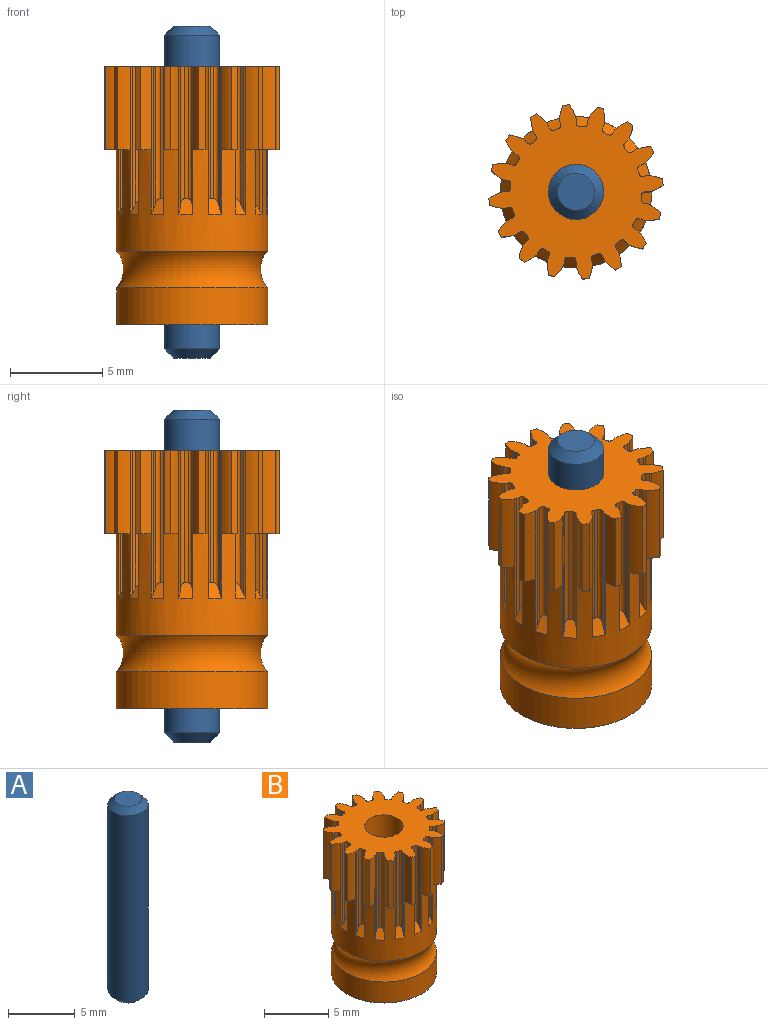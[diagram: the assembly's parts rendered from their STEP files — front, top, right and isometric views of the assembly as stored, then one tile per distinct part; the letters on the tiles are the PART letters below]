
ASSEMBLY  parts=2 mates=1
PART A: 5 faces, bbox 3x3x18 mm
  f0: cylinder r=1.5mm len=17mm, axis (0,0,-1), area 160.2mm2, adj f3,f4
  f1: plane 2x2mm, normal (0,0,1), area 3.1mm2, adj f4
  f2: plane 2x2mm, normal (0,0,-1), area 3.1mm2, adj f3
  f3: cone r=1.5mm half-angle=45deg, axis (0,0,1), area 5.6mm2, adj f0,f2
  f4: cone r=1mm half-angle=45deg, axis (0,0,-1), area 5.6mm2, adj f0,f1
PART B: 198 faces, bbox 9.5x9.5x14 mm
  f0: cylinder r=4.1mm len=8.2mm, axis (0,0,-1), area 100mm2, adj f5,f11,f12,f13,f19,f20,f26,f27
  f1: cylinder r=4.1mm len=8.2mm, axis (0,0,-1), area 51.5mm2, adj f4,f181
  f2: plane 9.45x9.45mm, normal (0,0,1), area 47mm2, adj f3,f5,f6,f7,f8,f9,f10,f11
  f3: cylinder r=1.5mm len=14mm, axis (0,0,-1), area 131.9mm2, adj f2,f4
  f4: plane 8.2x8.2mm, normal (0,0,-1), area 45.7mm2, adj f1,f3
  f5: plane 8x0.12mm, normal (0.97,0.24,0), area 1mm2, adj f0,f2,f6,f117,f188
  f6: plane 7.82x0.23mm, normal (1,0,0), area 1.8mm2, adj f2,f5,f7,f188
  f7: cylinder r=0.2mm len=7.46mm, axis (0,0,1), area 2.2mm2, adj f2,f6,f8,f188
  f8: plane 7.17x0.23mm, normal (0.09,1,0), area 1.6mm2, adj f2,f7,f9,f188
  f9: cylinder r=0.2mm len=7.46mm, axis (0,0,1), area 2.2mm2, adj f2,f8,f10,f188
  f10: plane 7.82x0.23mm, normal (-0.98,0.17,0), area 1.8mm2, adj f2,f9,f11,f188
  f11: plane 8x0.11mm, normal (-0.91,0.41,0), area 1mm2, adj f0,f2,f10,f177,f188
  f12: plane 8x0.09mm, normal (-0.69,0.73,0), area 1mm2, adj f0,f2,f18,f173,f189
  f13: plane 8x0.12mm, normal (0.99,-0.15,0), area 1mm2, adj f0,f2,f14,f178,f189
  f14: plane 7.82x0.21mm, normal (0.92,-0.38,0), area 1.8mm2, adj f2,f13,f15,f189
  f15: cylinder r=0.2mm len=7.46mm, axis (0,0,1), area 2.2mm2, adj f2,f14,f16,f189
  f16: plane 7.17x0.2mm, normal (0.46,0.89,0), area 1.6mm2, adj f2,f15,f17,f189
  f17: cylinder r=0.2mm len=7.46mm, axis (0,0,1), area 2.2mm2, adj f2,f16,f18,f189
  f18: plane 7.82x0.2mm, normal (-0.84,0.54,0), area 1.8mm2, adj f2,f12,f17,f189
  f19: plane 8x0.12mm, normal (-0.36,0.93,0), area 1mm2, adj f0,f2,f25,f169,f190
  f20: plane 8x0.11mm, normal (0.86,-0.52,0), area 1mm2, adj f0,f2,f21,f174,f190
  f21: plane 7.82x0.16mm, normal (0.71,-0.71,0), area 1.8mm2, adj f2,f20,f22,f190
  f22: cylinder r=0.2mm len=7.46mm, axis (0,0,1), area 2.2mm2, adj f2,f21,f23,f190
  f23: plane 7.17x0.18mm, normal (0.77,0.64,0), area 1.6mm2, adj f2,f22,f24,f190
  f24: cylinder r=0.2mm len=7.46mm, axis (0,0,1), area 2.2mm2, adj f2,f23,f25,f190
  f25: plane 7.82x0.19mm, normal (-0.57,0.82,0), area 1.8mm2, adj f2,f19,f24,f190
  f26: plane 8x0.12mm, normal (0.03,1,0), area 1mm2, adj f0,f2,f32,f165,f191
  f27: plane 8x0.1mm, normal (0.59,-0.8,0), area 1mm2, adj f0,f2,f28,f170,f191
  f28: plane 7.82x0.21mm, normal (0.38,-0.92,0), area 1.8mm2, adj f2,f27,f29,f191
  f29: cylinder r=0.2mm len=7.46mm, axis (0,0,1), area 2.2mm2, adj f2,f28,f30,f191
  f30: plane 7.17x0.22mm, normal (0.95,0.3,0), area 1.6mm2, adj f2,f29,f31,f191
  f31: cylinder r=0.2mm len=7.46mm, axis (0,0,1), area 2.2mm2, adj f2,f30,f32,f191
  f32: plane 7.82x0.23mm, normal (-0.22,0.98,0), area 1.8mm2, adj f2,f26,f31,f191
  f33: plane 8x0.11mm, normal (0.41,0.91,0), area 1mm2, adj f0,f2,f39,f161,f192
  f34: plane 8x0.12mm, normal (0.24,-0.97,0), area 1mm2, adj f0,f2,f35,f166,f192
  f35: plane 7.82x0.23mm, normal (0,-1,0), area 1.8mm2, adj f2,f34,f36,f192
  f36: cylinder r=0.2mm len=7.46mm, axis (0,0,1), area 2.2mm2, adj f2,f35,f37,f192
  f37: plane 7.17x0.23mm, normal (1,-0.09,0), area 1.6mm2, adj f2,f36,f38,f192
  f38: cylinder r=0.2mm len=7.46mm, axis (0,0,1), area 2.2mm2, adj f2,f37,f39,f192
  f39: plane 7.82x0.23mm, normal (0.17,0.98,0), area 1.8mm2, adj f2,f33,f38,f192
  f40: plane 8x0.09mm, normal (0.73,0.69,0), area 1mm2, adj f0,f2,f46,f157,f193
  f41: plane 8x0.12mm, normal (-0.15,-0.99,0), area 1mm2, adj f0,f2,f42,f162,f193
  f42: plane 7.82x0.21mm, normal (-0.38,-0.92,0), area 1.8mm2, adj f2,f41,f43,f193
  f43: cylinder r=0.2mm len=7.46mm, axis (0,0,1), area 2.2mm2, adj f2,f42,f44,f193
  f44: plane 7.17x0.2mm, normal (0.89,-0.46,0), area 1.6mm2, adj f2,f43,f45,f193
  f45: cylinder r=0.2mm len=7.46mm, axis (0,0,1), area 2.2mm2, adj f2,f44,f46,f193
  f46: plane 7.82x0.2mm, normal (0.54,0.84,0), area 1.8mm2, adj f2,f40,f45,f193
  f47: plane 8x0.12mm, normal (0.93,0.36,0), area 1mm2, adj f0,f2,f53,f153,f194
  f48: plane 8x0.11mm, normal (-0.52,-0.86,0), area 1mm2, adj f0,f2,f49,f158,f194
  f49: plane 7.82x0.16mm, normal (-0.71,-0.71,0), area 1.8mm2, adj f2,f48,f50,f194
  f50: cylinder r=0.2mm len=7.46mm, axis (0,0,1), area 2.2mm2, adj f2,f49,f51,f194
  f51: plane 7.17x0.18mm, normal (0.64,-0.77,0), area 1.6mm2, adj f2,f50,f52,f194
  f52: cylinder r=0.2mm len=7.46mm, axis (0,0,1), area 2.2mm2, adj f2,f51,f53,f194
  f53: plane 7.82x0.19mm, normal (0.82,0.57,0), area 1.8mm2, adj f2,f47,f52,f194
  f54: plane 8x0.12mm, normal (1,-0.03,0), area 1mm2, adj f0,f2,f60,f149,f195
  f55: plane 8x0.1mm, normal (-0.8,-0.59,0), area 1mm2, adj f0,f2,f56,f154,f195
  f56: plane 7.82x0.21mm, normal (-0.92,-0.38,0), area 1.8mm2, adj f2,f55,f57,f195
  f57: cylinder r=0.2mm len=7.46mm, axis (0,0,1), area 2.2mm2, adj f2,f56,f58,f195
  f58: plane 7.17x0.22mm, normal (0.3,-0.95,0), area 1.6mm2, adj f2,f57,f59,f195
  f59: cylinder r=0.2mm len=7.46mm, axis (0,0,1), area 2.2mm2, adj f2,f58,f60,f195
  f60: plane 7.82x0.23mm, normal (0.98,0.22,0), area 1.8mm2, adj f2,f54,f59,f195
  f61: plane 8x0.11mm, normal (0.91,-0.41,0), area 1mm2, adj f0,f2,f67,f145,f196
  f62: plane 8x0.12mm, normal (-0.97,-0.24,0), area 1mm2, adj f0,f2,f63,f150,f196
  f63: plane 7.82x0.23mm, normal (-1,0,0), area 1.8mm2, adj f2,f62,f64,f196
  f64: cylinder r=0.2mm len=7.46mm, axis (0,0,1), area 2.2mm2, adj f2,f63,f65,f196
  f65: plane 7.17x0.23mm, normal (-0.09,-1,0), area 1.6mm2, adj f2,f64,f66,f196
  f66: cylinder r=0.2mm len=7.46mm, axis (0,0,1), area 2.2mm2, adj f2,f65,f67,f196
  f67: plane 7.82x0.23mm, normal (0.98,-0.17,0), area 1.8mm2, adj f2,f61,f66,f196
  f68: plane 8x0.09mm, normal (0.69,-0.73,0), area 1mm2, adj f0,f2,f74,f141,f197
  f69: plane 8x0.12mm, normal (-0.99,0.15,0), area 1mm2, adj f0,f2,f70,f146,f197
  f70: plane 7.82x0.21mm, normal (-0.92,0.38,0), area 1.8mm2, adj f2,f69,f71,f197
  f71: cylinder r=0.2mm len=7.46mm, axis (0,0,1), area 2.2mm2, adj f2,f70,f72,f197
  f72: plane 7.17x0.2mm, normal (-0.46,-0.89,0), area 1.6mm2, adj f2,f71,f73,f197
  f73: cylinder r=0.2mm len=7.46mm, axis (0,0,1), area 2.2mm2, adj f2,f72,f74,f197
  f74: plane 7.82x0.2mm, normal (0.84,-0.54,0), area 1.8mm2, adj f2,f68,f73,f197
  f75: plane 8x0.12mm, normal (0.36,-0.93,0), area 1mm2, adj f0,f2,f81,f137,f182
  f76: plane 8x0.11mm, normal (-0.86,0.52,0), area 1mm2, adj f0,f2,f77,f142,f182
  f77: plane 7.82x0.16mm, normal (-0.71,0.71,0), area 1.8mm2, adj f2,f76,f78,f182
  f78: cylinder r=0.2mm len=7.46mm, axis (0,0,1), area 2.2mm2, adj f2,f77,f79,f182
  f79: plane 7.17x0.18mm, normal (-0.77,-0.64,0), area 1.6mm2, adj f2,f78,f80,f182
  f80: cylinder r=0.2mm len=7.46mm, axis (0,0,1), area 2.2mm2, adj f2,f79,f81,f182
  f81: plane 7.82x0.19mm, normal (0.57,-0.82,0), area 1.8mm2, adj f2,f75,f80,f182
  f82: plane 8x0.12mm, normal (-0.03,-1,0), area 1mm2, adj f0,f2,f88,f133,f183
  f83: plane 8x0.1mm, normal (-0.59,0.8,0), area 1mm2, adj f0,f2,f84,f138,f183
  f84: plane 7.82x0.21mm, normal (-0.38,0.92,0), area 1.8mm2, adj f2,f83,f85,f183
  f85: cylinder r=0.2mm len=7.46mm, axis (0,0,1), area 2.2mm2, adj f2,f84,f86,f183
  f86: plane 7.17x0.22mm, normal (-0.95,-0.3,0), area 1.6mm2, adj f2,f85,f87,f183
  f87: cylinder r=0.2mm len=7.46mm, axis (0,0,1), area 2.2mm2, adj f2,f86,f88,f183
  f88: plane 7.82x0.23mm, normal (0.22,-0.98,0), area 1.8mm2, adj f2,f82,f87,f183
  f89: plane 8x0.11mm, normal (-0.41,-0.91,0), area 1mm2, adj f0,f2,f95,f129,f184
  f90: plane 8x0.12mm, normal (-0.24,0.97,0), area 1mm2, adj f0,f2,f91,f134,f184
  f91: plane 7.82x0.23mm, normal (0,1,0), area 1.8mm2, adj f2,f90,f92,f184
  f92: cylinder r=0.2mm len=7.46mm, axis (0,0,1), area 2.2mm2, adj f2,f91,f93,f184
  f93: plane 7.17x0.23mm, normal (-1,0.09,0), area 1.6mm2, adj f2,f92,f94,f184
  f94: cylinder r=0.2mm len=7.46mm, axis (0,0,1), area 2.2mm2, adj f2,f93,f95,f184
  f95: plane 7.82x0.23mm, normal (-0.17,-0.98,0), area 1.8mm2, adj f2,f89,f94,f184
  f96: plane 8x0.09mm, normal (-0.73,-0.69,0), area 1mm2, adj f0,f2,f102,f125,f185
  f97: plane 8x0.12mm, normal (0.15,0.99,0), area 1mm2, adj f0,f2,f98,f130,f185
  f98: plane 7.82x0.21mm, normal (0.38,0.92,0), area 1.8mm2, adj f2,f97,f99,f185
  f99: cylinder r=0.2mm len=7.46mm, axis (0,0,1), area 2.2mm2, adj f2,f98,f100,f185
  f100: plane 7.17x0.2mm, normal (-0.89,0.46,0), area 1.6mm2, adj f2,f99,f101,f185
  f101: cylinder r=0.2mm len=7.46mm, axis (0,0,1), area 2.2mm2, adj f2,f100,f102,f185
  f102: plane 7.82x0.2mm, normal (-0.54,-0.84,0), area 1.8mm2, adj f2,f96,f101,f185
  f103: plane 8x0.12mm, normal (-0.93,-0.36,0), area 1mm2, adj f0,f2,f109,f121,f186
  f104: plane 8x0.11mm, normal (0.52,0.86,0), area 1mm2, adj f0,f2,f105,f126,f186
  f105: plane 7.82x0.16mm, normal (0.71,0.71,0), area 1.8mm2, adj f2,f104,f106,f186
  f106: cylinder r=0.2mm len=7.46mm, axis (0,0,1), area 2.2mm2, adj f2,f105,f107,f186
  f107: plane 7.17x0.18mm, normal (-0.64,0.77,0), area 1.6mm2, adj f2,f106,f108,f186
  f108: cylinder r=0.2mm len=7.46mm, axis (0,0,1), area 2.2mm2, adj f2,f107,f109,f186
  f109: plane 7.82x0.19mm, normal (-0.82,-0.57,0), area 1.8mm2, adj f2,f103,f108,f186
  f110: plane 8x0.12mm, normal (-1,0.03,0), area 1mm2, adj f0,f2,f116,f119,f187
  f111: plane 8x0.1mm, normal (0.8,0.59,0), area 1mm2, adj f0,f2,f112,f122,f187
  f112: plane 7.82x0.21mm, normal (0.92,0.38,0), area 1.8mm2, adj f2,f111,f113,f187
  f113: cylinder r=0.2mm len=7.46mm, axis (0,0,1), area 2.2mm2, adj f2,f112,f114,f187
  f114: plane 7.17x0.22mm, normal (-0.3,0.95,0), area 1.6mm2, adj f2,f113,f115,f187
  f115: cylinder r=0.2mm len=7.46mm, axis (0,0,1), area 2.2mm2, adj f2,f114,f116,f187
  f116: plane 7.82x0.23mm, normal (-0.98,-0.22,0), area 1.8mm2, adj f2,f110,f115,f187
  f117: cylinder r=2.4mm len=4.5mm, axis (0,0,1), area 3.2mm2, adj f2,f5,f118,f120
  f118: plane 4.5x0.35mm, normal (-0.11,0.99,0), area 1.6mm2, adj f2,f117,f119,f120
  f119: cylinder r=2.4mm len=4.5mm, axis (0,0,1), area 3.2mm2, adj f2,f110,f118,f120
  f120: plane 0.86x0.72mm, normal (0,0,-1), area 0.4mm2, adj f0,f117,f118,f119
  f121: cylinder r=2.4mm len=4.5mm, axis (0,0,1), area 3.2mm2, adj f2,f103,f123,f124
  f122: cylinder r=2.4mm len=4.5mm, axis (0,0,1), area 3.2mm2, adj f2,f111,f123,f124
  f123: plane 4.5x0.31mm, normal (-0.48,0.87,0), area 1.6mm2, adj f2,f121,f122,f124
  f124: plane 0.87x0.85mm, normal (0,0,-1), area 0.4mm2, adj f0,f121,f122,f123
  f125: cylinder r=2.4mm len=4.5mm, axis (0,0,1), area 3.2mm2, adj f2,f96,f127,f128
  f126: cylinder r=2.4mm len=4.5mm, axis (0,0,1), area 3.2mm2, adj f2,f104,f127,f128
  f127: plane 4.5x0.27mm, normal (-0.78,0.62,0), area 1.6mm2, adj f2,f125,f126,f128
  f128: plane 0.89x0.89mm, normal (0,0,-1), area 0.4mm2, adj f0,f125,f126,f127
  f129: cylinder r=2.4mm len=4.5mm, axis (0,0,1), area 3.2mm2, adj f2,f89,f131,f132
  f130: cylinder r=2.4mm len=4.5mm, axis (0,0,1), area 3.2mm2, adj f2,f97,f131,f132
  f131: plane 4.5x0.34mm, normal (-0.96,0.28,0), area 1.6mm2, adj f2,f129,f130,f132
  f132: plane 0.84x0.8mm, normal (0,0,-1), area 0.4mm2, adj f0,f129,f130,f131
  f133: cylinder r=2.4mm len=4.5mm, axis (0,0,1), area 3.2mm2, adj f2,f82,f135,f136
  f134: cylinder r=2.4mm len=4.5mm, axis (0,0,1), area 3.2mm2, adj f2,f90,f135,f136
  f135: plane 4.5x0.35mm, normal (-0.99,-0.11,0), area 1.6mm2, adj f2,f133,f134,f136
  f136: plane 0.86x0.72mm, normal (0,0,-1), area 0.4mm2, adj f0,f133,f134,f135
  f137: cylinder r=2.4mm len=4.5mm, axis (0,0,1), area 3.2mm2, adj f2,f75,f139,f140
  f138: cylinder r=2.4mm len=4.5mm, axis (0,0,1), area 3.2mm2, adj f2,f83,f139,f140
  f139: plane 4.5x0.31mm, normal (-0.87,-0.48,0), area 1.6mm2, adj f2,f137,f138,f140
  f140: plane 0.87x0.85mm, normal (0,0,-1), area 0.4mm2, adj f0,f137,f138,f139
  f141: cylinder r=2.4mm len=4.5mm, axis (0,0,1), area 3.2mm2, adj f2,f68,f143,f144
  f142: cylinder r=2.4mm len=4.5mm, axis (0,0,1), area 3.2mm2, adj f2,f76,f143,f144
  f143: plane 4.5x0.27mm, normal (-0.62,-0.78,0), area 1.6mm2, adj f2,f141,f142,f144
  f144: plane 0.89x0.89mm, normal (0,0,-1), area 0.4mm2, adj f0,f141,f142,f143
  f145: cylinder r=2.4mm len=4.5mm, axis (0,0,1), area 3.2mm2, adj f2,f61,f147,f148
  f146: cylinder r=2.4mm len=4.5mm, axis (0,0,1), area 3.2mm2, adj f2,f69,f147,f148
  f147: plane 4.5x0.34mm, normal (-0.28,-0.96,0), area 1.6mm2, adj f2,f145,f146,f148
  f148: plane 0.84x0.8mm, normal (0,0,-1), area 0.4mm2, adj f0,f145,f146,f147
  f149: cylinder r=2.4mm len=4.5mm, axis (0,0,1), area 3.2mm2, adj f2,f54,f151,f152
  f150: cylinder r=2.4mm len=4.5mm, axis (0,0,1), area 3.2mm2, adj f2,f62,f151,f152
  f151: plane 4.5x0.35mm, normal (0.11,-0.99,0), area 1.6mm2, adj f2,f149,f150,f152
  f152: plane 0.86x0.72mm, normal (0,0,-1), area 0.4mm2, adj f0,f149,f150,f151
  f153: cylinder r=2.4mm len=4.5mm, axis (0,0,1), area 3.2mm2, adj f2,f47,f155,f156
  f154: cylinder r=2.4mm len=4.5mm, axis (0,0,1), area 3.2mm2, adj f2,f55,f155,f156
  f155: plane 4.5x0.31mm, normal (0.48,-0.87,0), area 1.6mm2, adj f2,f153,f154,f156
  f156: plane 0.87x0.85mm, normal (0,0,-1), area 0.4mm2, adj f0,f153,f154,f155
  f157: cylinder r=2.4mm len=4.5mm, axis (0,0,1), area 3.2mm2, adj f2,f40,f159,f160
  f158: cylinder r=2.4mm len=4.5mm, axis (0,0,1), area 3.2mm2, adj f2,f48,f159,f160
  f159: plane 4.5x0.27mm, normal (0.78,-0.62,0), area 1.6mm2, adj f2,f157,f158,f160
  f160: plane 0.89x0.89mm, normal (0,0,-1), area 0.4mm2, adj f0,f157,f158,f159
  f161: cylinder r=2.4mm len=4.5mm, axis (0,0,1), area 3.2mm2, adj f2,f33,f163,f164
  f162: cylinder r=2.4mm len=4.5mm, axis (0,0,1), area 3.2mm2, adj f2,f41,f163,f164
  f163: plane 4.5x0.34mm, normal (0.96,-0.28,0), area 1.6mm2, adj f2,f161,f162,f164
  f164: plane 0.84x0.8mm, normal (0,0,-1), area 0.4mm2, adj f0,f161,f162,f163
  f165: cylinder r=2.4mm len=4.5mm, axis (0,0,1), area 3.2mm2, adj f2,f26,f167,f168
  f166: cylinder r=2.4mm len=4.5mm, axis (0,0,1), area 3.2mm2, adj f2,f34,f167,f168
  f167: plane 4.5x0.35mm, normal (0.99,0.11,0), area 1.6mm2, adj f2,f165,f166,f168
  f168: plane 0.86x0.72mm, normal (0,0,-1), area 0.4mm2, adj f0,f165,f166,f167
  f169: cylinder r=2.4mm len=4.5mm, axis (0,0,1), area 3.2mm2, adj f2,f19,f171,f172
  f170: cylinder r=2.4mm len=4.5mm, axis (0,0,1), area 3.2mm2, adj f2,f27,f171,f172
  f171: plane 4.5x0.31mm, normal (0.87,0.48,0), area 1.6mm2, adj f2,f169,f170,f172
  f172: plane 0.87x0.85mm, normal (0,0,-1), area 0.4mm2, adj f0,f169,f170,f171
  f173: cylinder r=2.4mm len=4.5mm, axis (0,0,1), area 3.2mm2, adj f2,f12,f175,f176
  f174: cylinder r=2.4mm len=4.5mm, axis (0,0,1), area 3.2mm2, adj f2,f20,f175,f176
  f175: plane 4.5x0.27mm, normal (0.62,0.78,0), area 1.6mm2, adj f2,f173,f174,f176
  f176: plane 0.89x0.89mm, normal (0,0,-1), area 0.4mm2, adj f0,f173,f174,f175
  f177: cylinder r=2.4mm len=4.5mm, axis (0,0,1), area 3.2mm2, adj f2,f11,f179,f180
  f178: cylinder r=2.4mm len=4.5mm, axis (0,0,1), area 3.2mm2, adj f2,f13,f179,f180
  f179: plane 4.5x0.34mm, normal (0.28,0.96,0), area 1.6mm2, adj f2,f177,f178,f180
  f180: plane 0.84x0.8mm, normal (0,0,-1), area 0.4mm2, adj f0,f177,f178,f179
  f181: torus R=5.22mm, axis (0,0,1), area 52.9mm2, adj f0,f1
  f182: cone r=3.45mm half-angle=33deg, axis (0,0,-1), area 0.6mm2, adj f0,f75,f76,f77,f78,f79,f80,f81
  f183: cone r=3.45mm half-angle=33deg, axis (0,0,-1), area 0.6mm2, adj f0,f82,f83,f84,f85,f86,f87,f88
  f184: cone r=3.45mm half-angle=33deg, axis (0,0,-1), area 0.6mm2, adj f0,f89,f90,f91,f92,f93,f94,f95
  f185: cone r=3.45mm half-angle=33deg, axis (0,0,-1), area 0.6mm2, adj f0,f96,f97,f98,f99,f100,f101,f102
  f186: cone r=3.45mm half-angle=33deg, axis (0,0,-1), area 0.6mm2, adj f0,f103,f104,f105,f106,f107,f108,f109
  f187: cone r=3.45mm half-angle=33deg, axis (0,0,-1), area 0.6mm2, adj f0,f110,f111,f112,f113,f114,f115,f116
  f188: cone r=3.45mm half-angle=33deg, axis (0,0,-1), area 0.6mm2, adj f0,f5,f6,f7,f8,f9,f10,f11
  f189: cone r=3.45mm half-angle=33deg, axis (0,0,-1), area 0.6mm2, adj f0,f12,f13,f14,f15,f16,f17,f18
  f190: cone r=3.45mm half-angle=33deg, axis (0,0,-1), area 0.6mm2, adj f0,f19,f20,f21,f22,f23,f24,f25
  f191: cone r=3.45mm half-angle=33deg, axis (0,0,-1), area 0.6mm2, adj f0,f26,f27,f28,f29,f30,f31,f32
  f192: cone r=3.45mm half-angle=33deg, axis (0,0,-1), area 0.6mm2, adj f0,f33,f34,f35,f36,f37,f38,f39
  f193: cone r=3.45mm half-angle=33deg, axis (0,0,-1), area 0.6mm2, adj f0,f40,f41,f42,f43,f44,f45,f46
  f194: cone r=3.45mm half-angle=33deg, axis (0,0,-1), area 0.6mm2, adj f0,f47,f48,f49,f50,f51,f52,f53
  f195: cone r=3.45mm half-angle=33deg, axis (0,0,-1), area 0.6mm2, adj f0,f54,f55,f56,f57,f58,f59,f60
  f196: cone r=3.45mm half-angle=33deg, axis (0,0,-1), area 0.6mm2, adj f0,f61,f62,f63,f64,f65,f66,f67
  f197: cone r=3.45mm half-angle=33deg, axis (0,0,-1), area 0.6mm2, adj f0,f68,f69,f70,f71,f72,f73,f74
PLACE A t=(-2.36,1.41,-4.87)mm fixed
PLACE B t=(-2.36,1.41,-3.07)mm
MATE fastened A.f0 <-> B.f3  axis (0,0,1) through (-2.36,1.41,13.13)mm
